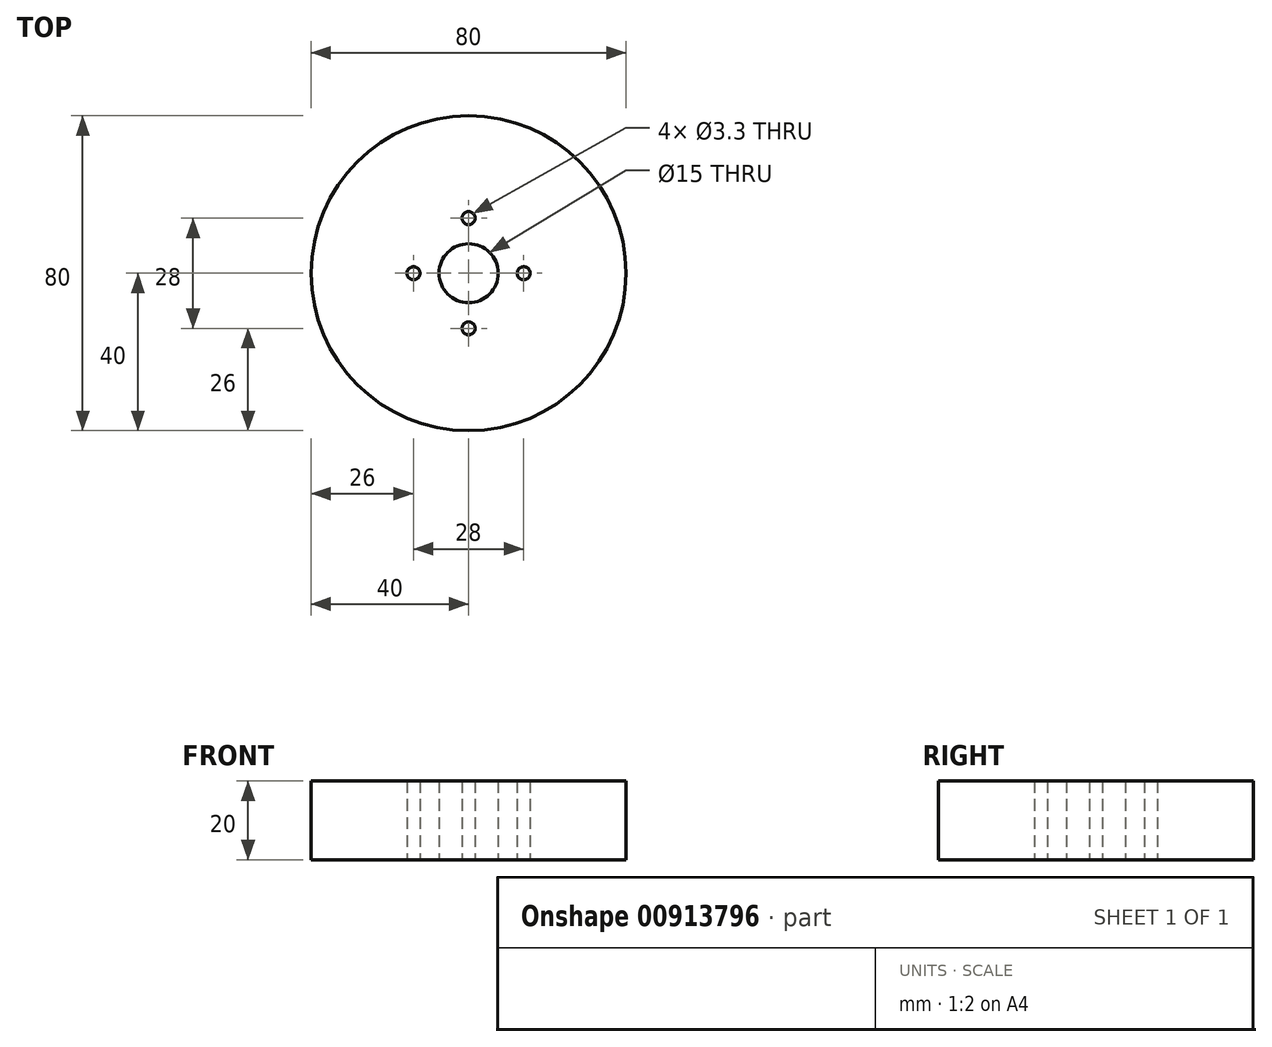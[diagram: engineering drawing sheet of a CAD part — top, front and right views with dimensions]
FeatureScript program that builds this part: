
annotation { "Feature Type Name" : "Feature", "Feature Type Description" : "" }
export const myFeature = defineFeature(function(context is Context, id is Id, definition is map)
    precondition{}
    {
        {
            var Q0;
            Q0=qCreatedBy(makeId("Top.planeOp"),FACE);
            var sketch = newSketch(context, id + "F0", { "sketchPlane" : qUnion([Q0])});
            skCircle(sketch, "E0", {"center": v(0, 0) * mm, "radius": 40 * mm});
            skCircle(sketch, "E1", {"center": v(0, 0) * mm, "radius": 7.5 * mm});
            skSolve(sketch);
        }
        {
            var Q0;
            Q0=qCreatedBy(makeId("Top.planeOp"),FACE);
            var sketch = newSketch(context, id + "F1", { "sketchPlane" : qUnion([Q0])});
            skCircle(sketch, "E2", {"center": v(0, -14) * mm, "radius": 1.65 * mm});
            skCircle(sketch, "E3", {"center": v(14, 0) * mm, "radius": 1.65 * mm});
            skCircle(sketch, "E4", {"center": v(0, 14) * mm, "radius": 1.65 * mm});
            skCircle(sketch, "E5", {"center": v(-14, 0) * mm, "radius": 1.65 * mm});
            skSolve(sketch);
        }
        {
            var Q0;
            Q0 = qSketchRegion(id + "F0", true);
            extrude(context, id + "F2", {"entities" : qUnion([Q0]), "depth" : 20 * mm, "offsetDistance" : 25 * mm});
        }
        {
            var Q0;
            Q0 = qSketchRegion(id + "F1", true);
            extrude(context, id + "F3", {"entities" : qUnion([Q0]), "operationType" : NewBodyOperationType.REMOVE, "depth" : 20 * mm, "offsetDistance" : 25 * mm});
        }
    });
